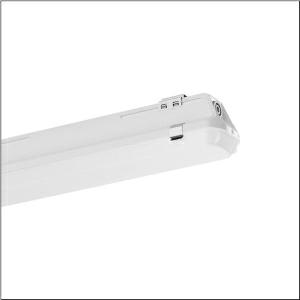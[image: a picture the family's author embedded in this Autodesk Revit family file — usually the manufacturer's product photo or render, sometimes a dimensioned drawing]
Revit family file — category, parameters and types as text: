
# Revit family: monsun_r__11_emergency_51fp10dp467h3h_d298
name_source: partatom
category: Lighting Fixtures
units: mm (PartAtom-declared; Revit-internal decimal feet)

## family parameters
Cut with Voids When Loaded = No
Host = Face
Light Source = No
Part Type = Normal
Room Calculation Point = No
Round Connector Dimension = Use Diameter
Shared = No

## types (1)
- --- (1 x LED, 870 lm, 5 W, 4000K)
    Apparent Load = 5 VA
    CIE Flux Codes = 47 77 93 94 100
    Color Rendering = 80
    Color Temperature = 4000K
    Default Elevation = 1800 mm
    Description = Monsun® 11 emergency, damp-proof luminaire, chain hanger, primary optical cover: enclosure, of PMMA, light emission: direct distribution, primary light characteristic: symmetric, installation type: suspended mounting, surface-mounted, horizontal mounting, vertical mounting, LED, rated luminous flux: 6.050lm, luminous efficacy: 175lm/W, light colour: 840, colour temperature: 4000K, control gear: ECG DALI, with terminal, 5+3-pole, max. 2.5mm², mains connection: 220..240V, AC, 50/60Hz, rated input power: 35W, control gear: single battery element, battery: NiCd, 4,5Ah, mains connection: 230V, 50Hz, luminaire housing, of glass-fibre reinforced polyester, uncoated, bright grey, incl. chain hanger, length: 1.590mm, width: 90mm, height: 88mm, clip for enclosure, of stainless steel (V2A), ceiling mounting element, of stainless steel (V2A), chain hanger, of stainless steel (V2A), protection rating (complete): IP66, insulation class (complete): insulation class I (protective earthing), certification: CE, UKCA, protection symbol: D, impact resistance: IK04, permissible operating ambient temperature: +5..+35°C, standard: EN 50419, EN 60598-2-1, EN 60598-2-22, no direct snow, no direct sun, no direct rain, for indoor or canopied outdoor use, corresponds to IFS (International Featured Standards) requirements for safety and quality in the food industry, contact your sales advisor before using the luminaires in applications with unclear chemical exposure, large temperature fluctuations or condensation-forming humidity, LABS conformity tested according to VDMA 24364:2018-05, packaging unit: 1 piece
    Height = 89 mm
    Lamp = 1 x LED
    Lamp Light Flux = 870 lm
    Lamp Power = 5 W
    Lamp count = 1
    Length = 1590 mm
    Luminous efficacy = 174 lm/W
    Manufacturer = Siteco
    ModVariant = No
    Model = 51FP10DP467H3H
    Mounting Place = Ceiling
    Mounting Type = Surface mounted
    Number of Poles = 1
    OnlyDefault = Yes
    Power Factor = 1
    Product Name = Monsun® 11 emergency
    Product group = damp-proof luminaire
    ProductGroupID = 301
    Protection Class = Protection class I
    Protection Degree = IP 66
    RLX_Detail_Level = 1
    RLX_Emergency_Light_Flux = 0 lm
    RLX_Emergency_Type = 0
    RLX_Emergency_Type_DB = No
    RlxData = <blob elided: 92385 chars, md5=2c6d4931>
    Socket = socket
    Standby Power = 0 W
    System Light Flux = 870 lm
    System Power = 5 W
    Type Comments = : emergency light operation: 3 h
    Type Image = l_1004748.jpg
    URL = http://relux.com
    VarID = @adj_152535
    Voltage = 0 V
    Weight = 0.00 kg
    Width = 90 mm

## geometry (parser evidence)
native form markers: Blend x4, Sweep x14
no freeform markers — native parametric forms only
